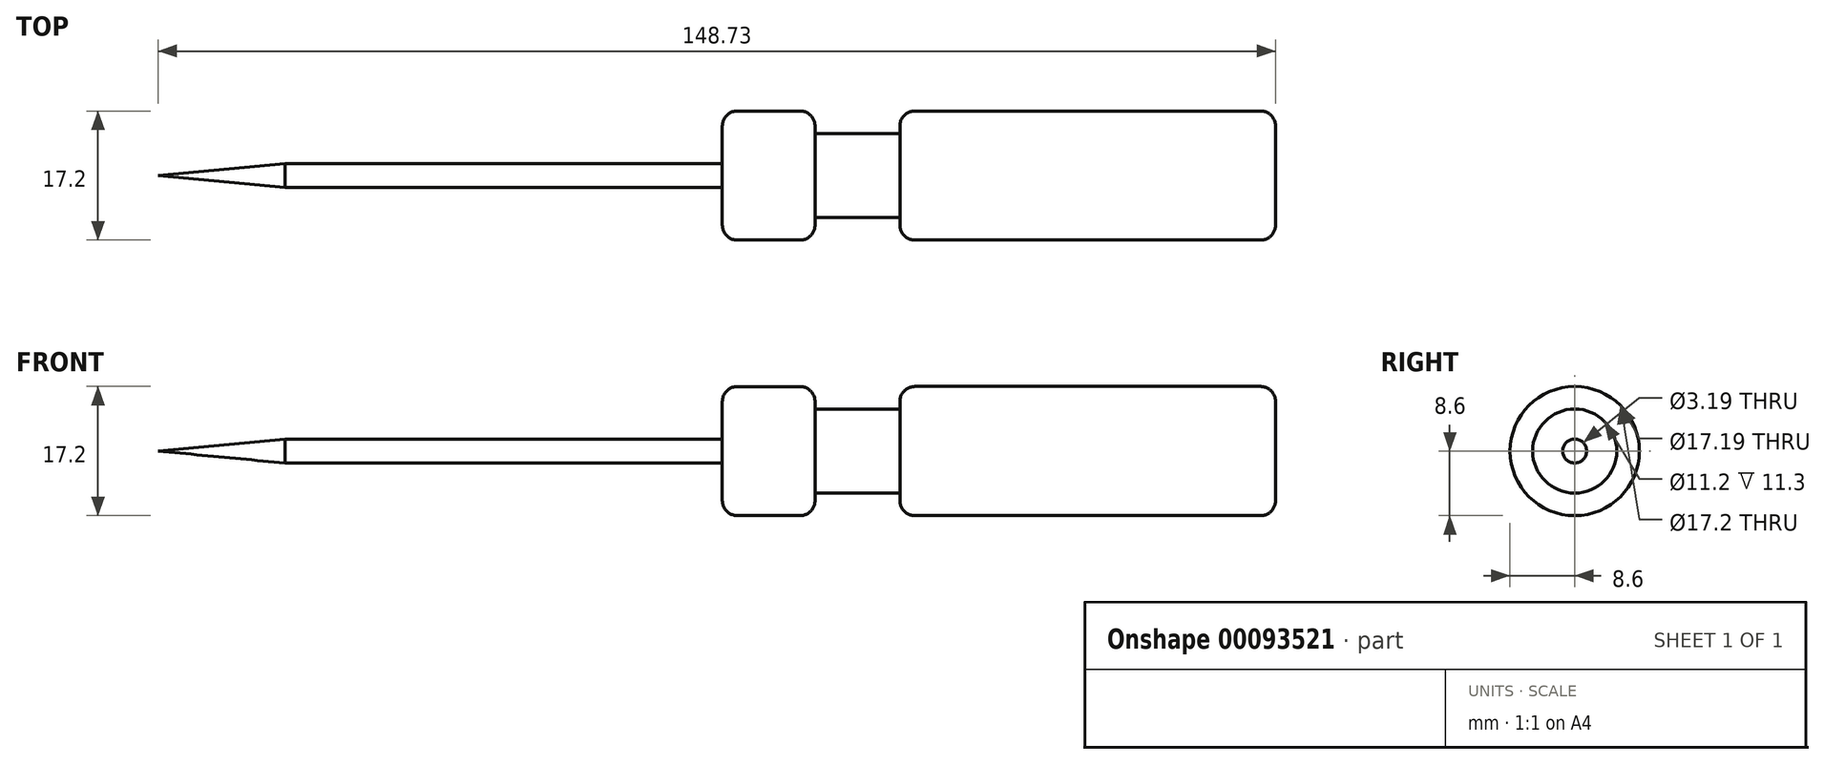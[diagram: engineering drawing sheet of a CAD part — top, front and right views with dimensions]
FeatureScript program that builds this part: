
annotation { "Feature Type Name" : "Feature", "Feature Type Description" : "" }
export const myFeature = defineFeature(function(context is Context, id is Id, definition is map)
    precondition{}
    {
        {
            var Q0;
            Q0=qCreatedBy(makeId("Front.planeOp"),FACE);
            var sketch = newSketch(context, id + "F0", { "sketchPlane" : qUnion([Q0])});
            skLineSegment(sketch, "E0", {"start": v(83.62, 0) * mm, "end": v(-65.11, 0) * mm, "construction": true});
            skLineSegment(sketch, "E1", {"start": v(83.62, 0) * mm, "end": v(83.62, 8.6) * mm});
            skLineSegment(sketch, "E2", {"start": v(83.62, 8.6) * mm, "end": v(33.62, 8.6) * mm});
            skLineSegment(sketch, "E3", {"start": v(33.62, 8.6) * mm, "end": v(33.62, 5.6) * mm});
            skLineSegment(sketch, "E4", {"start": v(33.62, 5.6) * mm, "end": v(22.32, 5.6) * mm});
            skLineSegment(sketch, "E5", {"start": v(22.32, 5.6) * mm, "end": v(22.32, 8.6) * mm});
            skLineSegment(sketch, "E6", {"start": v(22.32, 8.6) * mm, "end": v(9.99, 8.6) * mm});
            skLineSegment(sketch, "E7", {"start": v(9.99, 8.6) * mm, "end": v(9.99, 1.6) * mm});
            skLineSegment(sketch, "E8", {"start": v(9.99, 1.6) * mm, "end": v(-48.21, 1.6) * mm});
            skLineSegment(sketch, "E9", {"start": v(-48.21, 1.6) * mm, "end": v(-65.11, 0) * mm});
            skSolve(sketch);
        }
        {
            var Q0;
            Q0=sQuery(id+"F0.wireOp",EDGE,"E2");
            var Q1;
            Q1=sQuery(id+"F0.wireOp",EDGE,"E1");
            var Q2;
            Q2=sQuery(id+"F0.wireOp",EDGE,"E4");
            var Q3;
            Q3=sQuery(id+"F0.wireOp",EDGE,"E3");
            var Q4;
            Q4=sQuery(id+"F0.wireOp",EDGE,"E5");
            var Q5;
            Q5=sQuery(id+"F0.wireOp",EDGE,"E6");
            var Q6;
            Q6=sQuery(id+"F0.wireOp",EDGE,"E7");
            var Q7;
            Q7=sQuery(id+"F0.wireOp",EDGE,"E8");
            var Q8;
            Q8=sQuery(id+"F0.wireOp",EDGE,"E9");
            var Q9;
            Q9=sQuery(id+"F0.wireOp",EDGE,"E0");
            revolve(context, id + "F1", {"bodyType" : ToolBodyType.SURFACE, "surfaceEntities" : qUnion([Q0, Q1, Q2, Q3, Q4, Q5, Q6, Q7, Q8]), "axis" : qUnion([Q9]), "revolveType" : RevolveType.FULL});
        }
        {
            var Q0;
            Q0=makeQuery(id+"F1.opRevolve","SWEPT_EDGE",EDGE,{"disambiguationData":[OSD([sQuery(id+"F0.wireOp",VERTEX,"E7.start")])]});
            fillet(context, id + "F2", {"entities" : qUnion([Q0]), "radius" : 2 * mm, "tangentPropagation" : true, "allowEdgeOverflow" : false});
        }
        {
            var Q0;
            Q0=makeQuery(id+"F1.opRevolve","SWEPT_EDGE",EDGE,{"disambiguationData":[OSD([sQuery(id+"F0.wireOp",VERTEX,"E6.start")])]});
            var Q1;
            Q1=makeQuery(id+"F1.opRevolve","SWEPT_EDGE",EDGE,{"disambiguationData":[OSD([sQuery(id+"F0.wireOp",VERTEX,"E3.start")])]});
            var Q2;
            Q2=makeQuery(id+"F1.opRevolve","SWEPT_EDGE",EDGE,{"disambiguationData":[OSD([sQuery(id+"F0.wireOp",VERTEX,"E1.end")])]});
            fillet(context, id + "F3", {"entities" : qUnion([Q0, Q1, Q2]), "radius" : 2 * mm, "tangentPropagation" : true, "allowEdgeOverflow" : false});
        }
    });
